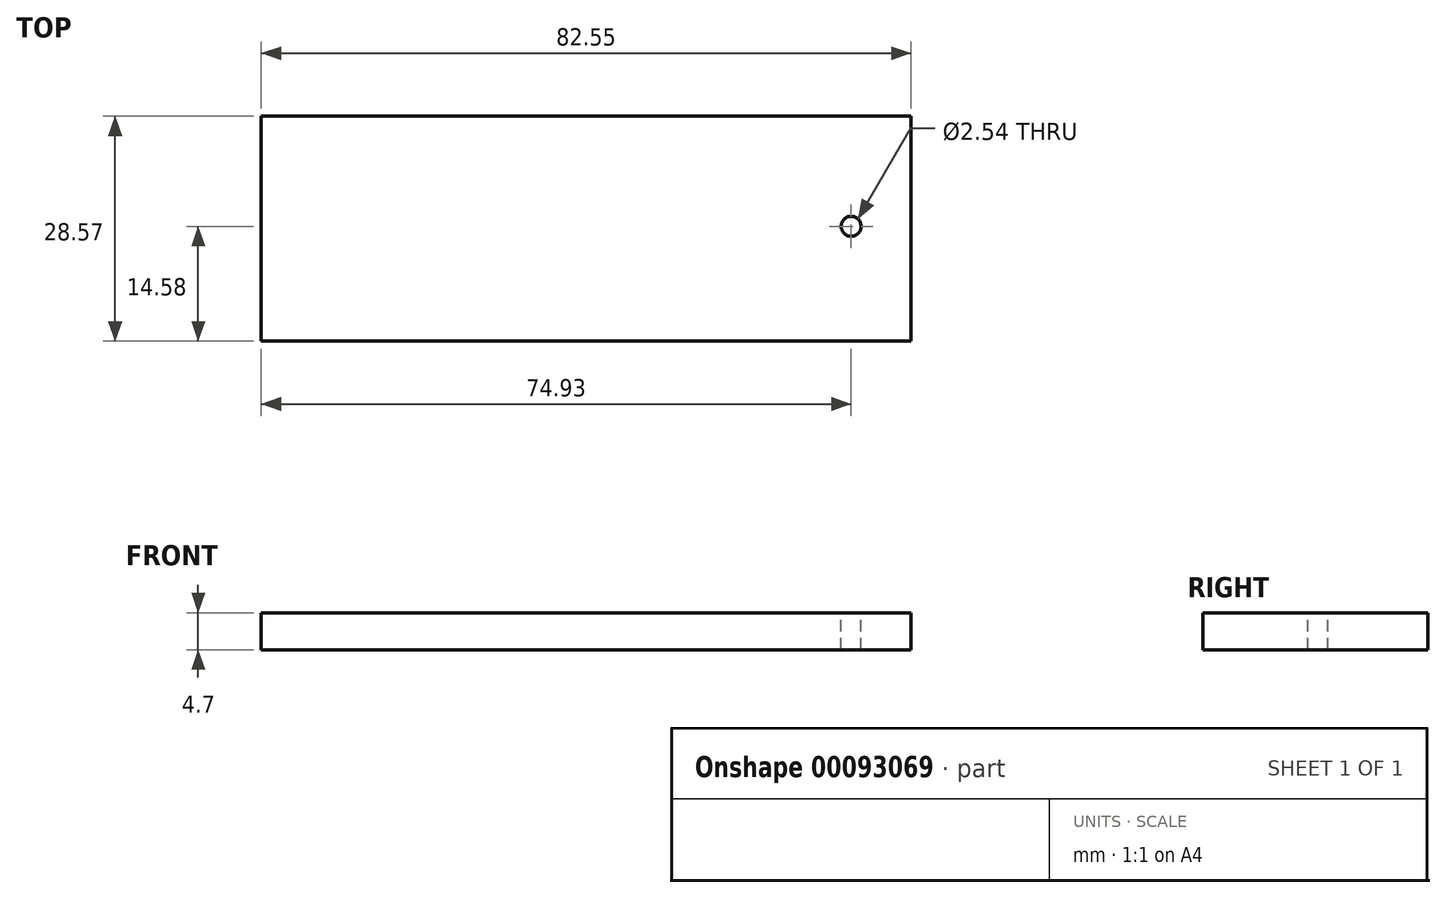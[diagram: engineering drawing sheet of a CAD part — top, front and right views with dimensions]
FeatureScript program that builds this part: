
annotation { "Feature Type Name" : "Feature", "Feature Type Description" : "" }
export const myFeature = defineFeature(function(context is Context, id is Id, definition is map)
    precondition{}
    {
        {
            var Q0;
            Q0=qCreatedBy(makeId("Top.planeOp"),FACE);
            var sketch = newSketch(context, id + "F0", { "sketchPlane" : qUnion([Q0])});
            skLineSegment(sketch, "E0.bottom", {"start": v(0, 14) * mm, "end": v(-82.55, 14) * mm});
            skLineSegment(sketch, "E0.top", {"start": v(0, -14.58) * mm, "end": v(-82.55, -14.58) * mm});
            skLineSegment(sketch, "E0.left", {"start": v(0, 14) * mm, "end": v(0, -14.58) * mm});
            skLineSegment(sketch, "E0.right", {"start": v(-82.55, 14) * mm, "end": v(-82.55, -14.58) * mm});
            skSolve(sketch);
        }
        {
            var Q0;
            Q0=qSketchRegion(id+"F0",true);
            extrude(context, id + "F1", {"entities" : qUnion([Q0]), "depth" : 4.7 * mm});
        }
        {
            var Q0;
            Q0=makeQuery(id+"F1.opExtrude","CAP_FACE",FACE,{"disambiguationData":[OSD([sQuery(id+"F0.wireOp",EDGE,"E0.bottom"),sQuery(id+"F0.wireOp",EDGE,"E0.top"),sQuery(id+"F0.wireOp",EDGE,"E0.left"),sQuery(id+"F0.wireOp",EDGE,"E0.right")])],"isStart":false});
            var sketch = newSketch(context, id + "F2", { "sketchPlane" : qUnion([Q0])});
            skCircle(sketch, "E1", {"center": v(-7.62, 0) * mm, "radius": 1.27 * mm});
            skSolve(sketch);
        }
        {
            var Q0;
            Q0=qSketchRegion(id+"F2",true);
            extrude(context, id + "F3", {"entities" : qUnion([Q0]), "operationType" : NewBodyOperationType.REMOVE, "endBound" : BoundingType.THROUGH_ALL, "oppositeDirection" : true, "depth" : 25.4 * mm});
        }
    });
